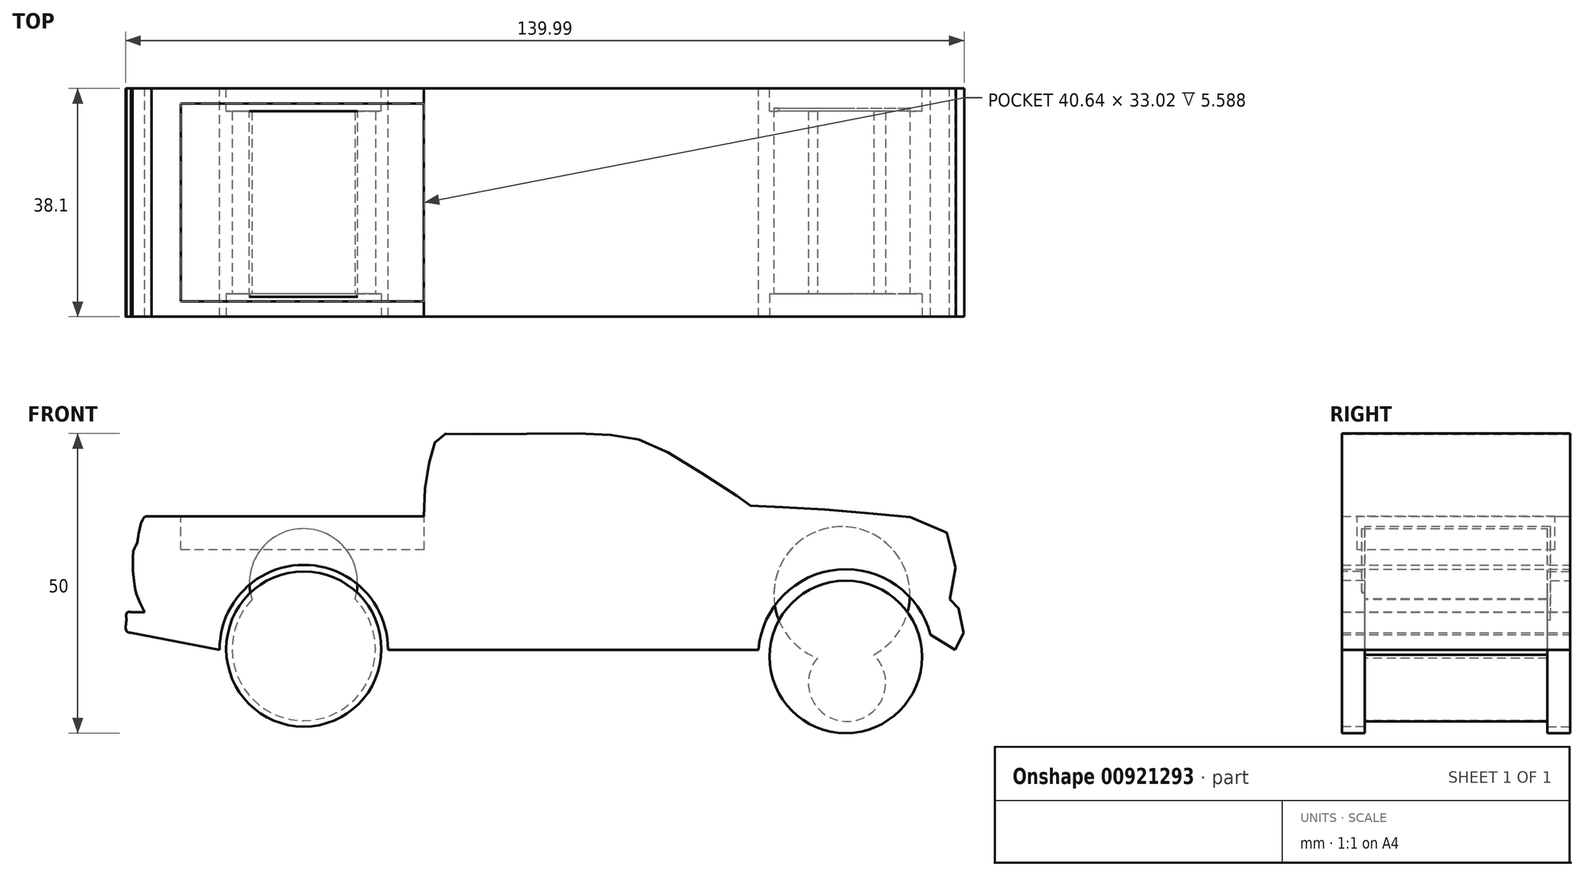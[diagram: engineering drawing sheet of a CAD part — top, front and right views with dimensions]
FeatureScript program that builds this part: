
annotation { "Feature Type Name" : "Feature", "Feature Type Description" : "" }
export const myFeature = defineFeature(function(context is Context, id is Id, definition is map)
    precondition{}
    {
        {
            var Q0;
            Q0=qCreatedBy(makeId("Front.planeOp"),FACE);
            var sketch = newSketch(context, id + "F0", { "sketchPlane" : qUnion([Q0])});
            skLineSegment(sketch, "E0", {"start": v(-69.28, -5.05) * mm, "end": v(-54.44, -7.9) * mm});
            skArc(sketch, "E1", {"start": v(-26.35, -7.9) * mm, "mid": v(-40.4, 6.31) * mm, "end": v(-54.44, -7.9) * mm});
            skLineSegment(sketch, "E2", {"start": v(-26.35, -7.9) * mm, "end": v(35.5, -7.9) * mm});
            skArc(sketch, "E3", {"start": v(64.23, -5.37) * mm, "mid": v(48.8, 5.52) * mm, "end": v(35.5, -7.9) * mm});
            skLineSegment(sketch, "E4", {"start": v(64.23, -5.37) * mm, "end": v(68.33, -7.9) * mm});
            skFitSpline(sketch, "E5", {"points": [v(68.33, -7.9) * mm, v(69.38, -6.41) * mm, v(69.33, -1.25) * mm, v(67.6, -0.59) * mm, v(67.98, 2.63) * mm, v(66.92, 11.71) * mm, v(54.4, 14.88) * mm, v(42.45, 15.83) * mm, v(34.05, 16.2) * mm, v(33.8, 16.47) * mm, v(26.75, 21.16) * mm, v(17.77, 26.41) * mm, v(11.79, 27.91) * mm, v(3.15, 28.23) * mm, v(-15.04, 28.17) * mm, v(-17.24, 28.1) * mm, v(-18.34, 27.09) * mm, v(-19.19, 24.5) * mm, v(-20.06, 19.98) * mm, v(-20.36, 14.4) * mm], "startDerivative": vector(37.65, 32.41) * mm, "endDerivative": vector(-2.3, -108.14) * mm});
            skLineSegment(sketch, "E6", {"start": v(-20.36, 14.4) * mm, "end": v(-65.83, 14.4) * mm});
            skFitSpline(sketch, "E7", {"points": [v(-65.83, 14.4) * mm, v(-66.62, 14.4) * mm, v(-67.11, 14.18) * mm, v(-67.88, 12) * mm, v(-68.38, 9.57) * mm, v(-68.8, 8.91) * mm, v(-68.85, 4.5) * mm, v(-68.2, 1.02) * mm, v(-66.98, -1.56) * mm], "startDerivative": vector(-10.65, 0.35) * mm, "endDerivative": vector(9.08, -16.9) * mm});
            skLineSegment(sketch, "E8", {"start": v(-66.98, -1.56) * mm, "end": v(-69.28, -1.56) * mm});
            skFitSpline(sketch, "E9", {"points": [v(-69.28, -1.56) * mm, v(-69.94, -1.69) * mm, v(-70.04, -3) * mm, v(-70.05, -4.66) * mm, v(-69.28, -5.05) * mm], "startDerivative": vector(-3.85, 0.31) * mm, "endDerivative": vector(4.27, -0.96) * mm});
            skSolve(sketch);
        }
        {
            var Q0;
            Q0=qSketchRegion(id+"F0",true);
            extrude(context, id + "F1", {"entities" : qUnion([Q0]), "endBound" : BoundingType.SYMMETRIC, "depth" : 38.1 * mm, "offsetDistance" : 25.4 * mm});
        }
        {
            var Q0;
            Q0=makeQuery(id+"F1.opExtrude","SWEPT_FACE",FACE,{"disambiguationData":[OSD([sQuery(id+"F0.wireOp",EDGE,"E6")])]});
            var sketch = newSketch(context, id + "F2", { "sketchPlane" : qUnion([Q0])});
            skLineSegment(sketch, "E10.bottom", {"start": v(-20.33, 16.51) * mm, "end": v(-60.97, 16.51) * mm});
            skLineSegment(sketch, "E10.top", {"start": v(-20.33, -16.5) * mm, "end": v(-60.97, -16.51) * mm});
            skLineSegment(sketch, "E10.left", {"start": v(-20.33, 16.51) * mm, "end": v(-20.33, -16.5) * mm});
            skLineSegment(sketch, "E10.right", {"start": v(-60.97, 16.51) * mm, "end": v(-60.97, -16.51) * mm});
            skSolve(sketch);
        }
        {
            var Q0;
            Q0=qSketchRegion(id+"F2",true);
            extrude(context, id + "F3", {"entities" : qUnion([Q0]), "operationType" : NewBodyOperationType.REMOVE, "oppositeDirection" : true, "depth" : 5.6 * mm, "offsetDistance" : 25.4 * mm});
        }
        {
            var Q0;
            Q0=makeQuery(id+"F1.opExtrude","CAP_FACE",FACE,{"disambiguationData":[OSD([sQuery(id+"F0.wireOp",EDGE,"E0"),sQuery(id+"F0.wireOp",EDGE,"E1"),sQuery(id+"F0.wireOp",EDGE,"E2"),sQuery(id+"F0.wireOp",EDGE,"E3"),sQuery(id+"F0.wireOp",EDGE,"E4"),sQuery(id+"F0.wireOp",EDGE,"E5"),sQuery(id+"F0.wireOp",EDGE,"E6"),sQuery(id+"F0.wireOp",EDGE,"E7"),sQuery(id+"F0.wireOp",EDGE,"E8"),sQuery(id+"F0.wireOp",EDGE,"E9")])],"isStart":true});
            var sketch = newSketch(context, id + "F4", { "sketchPlane" : qUnion([Q0])});
            skCircle(sketch, "E11", {"center": v(40.4, -7.73) * mm, "radius": 12.95 * mm});
            skCircle(sketch, "E12", {"center": v(-50.08, -9.04) * mm, "radius": 12.73 * mm});
            skSolve(sketch);
        }
        {
            var Q0;
            Q0=qSketchRegion(id+"F4",true);
            extrude(context, id + "F5", {"entities" : qUnion([Q0]), "oppositeDirection" : true, "depth" : 3.8 * mm, "offsetDistance" : 25.4 * mm});
        }
        {
            var Q0;
            Q0=makeQuery(id+"F5.opExtrude","SWEPT_BODY",BODY,{"disambiguationData":[OSD([sQuery(id+"F4.wireOp",EDGE,"E11")])]});
            var Q1;
            Q1=makeQuery(id+"F5.opExtrude","SWEPT_BODY",BODY,{"disambiguationData":[OSD([sQuery(id+"F4.wireOp",EDGE,"E12")])]});
            var Q2;
            Q2=qCreatedBy(makeId("Front.planeOp"),FACE);
            mirror(context, id + "F6", {"entities" : qUnion([Q0, Q1]), "mirrorPlane" : qUnion([Q2])});
        }
        {
            var Q0;
            Q0=makeQuery(id+"F6.opPattern","COPY",FACE,{"derivedFrom":makeQuery(id+"F5.opExtrude","CAP_FACE",FACE,{"disambiguationData":[OSD([sQuery(id+"F4.wireOp",EDGE,"E11")])],"isStart":true}),"instanceName":"1"});
            var sketch = newSketch(context, id + "F7", { "sketchPlane" : qUnion([Q0])});
            skCircle(sketch, "E13", {"center": v(-40.4, -7.73) * mm, "radius": 7.04 * mm});
            skSolve(sketch);
        }
        {
            var Q0;
            Q0=makeQuery(id+"F6.opPattern","COPY",FACE,{"derivedFrom":makeQuery(id+"F5.opExtrude","CAP_FACE",FACE,{"disambiguationData":[OSD([sQuery(id+"F4.wireOp",EDGE,"E12")])],"isStart":true}),"instanceName":"1"});
            var sketch = newSketch(context, id + "F8", { "sketchPlane" : qUnion([Q0])});
            skSolve(sketch);
        }
        {
            var Q0;
            Q0=makeQuery(id+"F5.opExtrude","CAP_FACE",FACE,{"disambiguationData":[OSD([sQuery(id+"F4.wireOp",EDGE,"E11")])],"isStart":false});
            var sketch = newSketch(context, id + "F9", { "sketchPlane" : qUnion([Q0])});
            skCircle(sketch, "E14", {"center": v(-40.46, 3.33) * mm, "radius": 9.02 * mm});
            skSolve(sketch);
        }
        {
            var Q0;
            Q0 = qSketchRegion(id + "F9", true);
            extrude(context, id + "F10", {"entities" : qUnion([Q0]), "depth" : 30.99 * mm, "offsetDistance" : 25.4 * mm});
        }
        {
            var Q0;
            Q0=makeQuery(id+"F6.opPattern","COPY",FACE,{"derivedFrom":makeQuery(id+"F5.opExtrude","CAP_FACE",FACE,{"disambiguationData":[OSD([sQuery(id+"F4.wireOp",EDGE,"E12")])],"isStart":false}),"instanceName":"1"});
            var sketch = newSketch(context, id + "F11", { "sketchPlane" : qUnion([Q0])});
            skCircle(sketch, "E15", {"center": v(-49.44, 1.34) * mm, "radius": 11.35 * mm});
            skSolve(sketch);
        }
        {
            var Q0;
            Q0 = qSketchRegion(id + "F11", true);
            extrude(context, id + "F12", {"entities" : qUnion([Q0]), "depth" : 30.99 * mm, "offsetDistance" : 25.4 * mm});
        }
        {
            var Q0;
            Q0=makeQuery(id+"F6.opPattern","COPY",FACE,{"derivedFrom":makeQuery(id+"F5.opExtrude","CAP_FACE",FACE,{"disambiguationData":[OSD([sQuery(id+"F4.wireOp",EDGE,"E11")])],"isStart":false}),"instanceName":"1"});
            var sketch = newSketch(context, id + "F13", { "sketchPlane" : qUnion([Q0])});
            skCircle(sketch, "E16", {"center": v(40.4, -7.73) * mm, "radius": 11.96 * mm});
            skSolve(sketch);
        }
        {
            var Q0;
            Q0 = qSketchRegion(id + "F13", true);
            extrude(context, id + "F14", {"entities" : qUnion([Q0]), "operationType" : NewBodyOperationType.ADD, "depth" : 32.26 * mm, "offsetDistance" : 25.4 * mm});
        }
        {
            var Q0;
            Q0=makeQuery(id+"F6.opPattern","COPY",FACE,{"derivedFrom":makeQuery(id+"F5.opExtrude","CAP_FACE",FACE,{"disambiguationData":[OSD([sQuery(id+"F4.wireOp",EDGE,"E12")])],"isStart":false}),"instanceName":"1"});
            var sketch = newSketch(context, id + "F15", { "sketchPlane" : qUnion([Q0])});
            skCircle(sketch, "E17", {"center": v(-50.3, -13.37) * mm, "radius": 6.46 * mm});
            skSolve(sketch);
        }
        {
            var Q0;
            Q0 = qSketchRegion(id + "F15", true);
            extrude(context, id + "F16", {"entities" : qUnion([Q0]), "operationType" : NewBodyOperationType.ADD, "depth" : 30.73 * mm, "offsetDistance" : 25.4 * mm});
        }
    });
